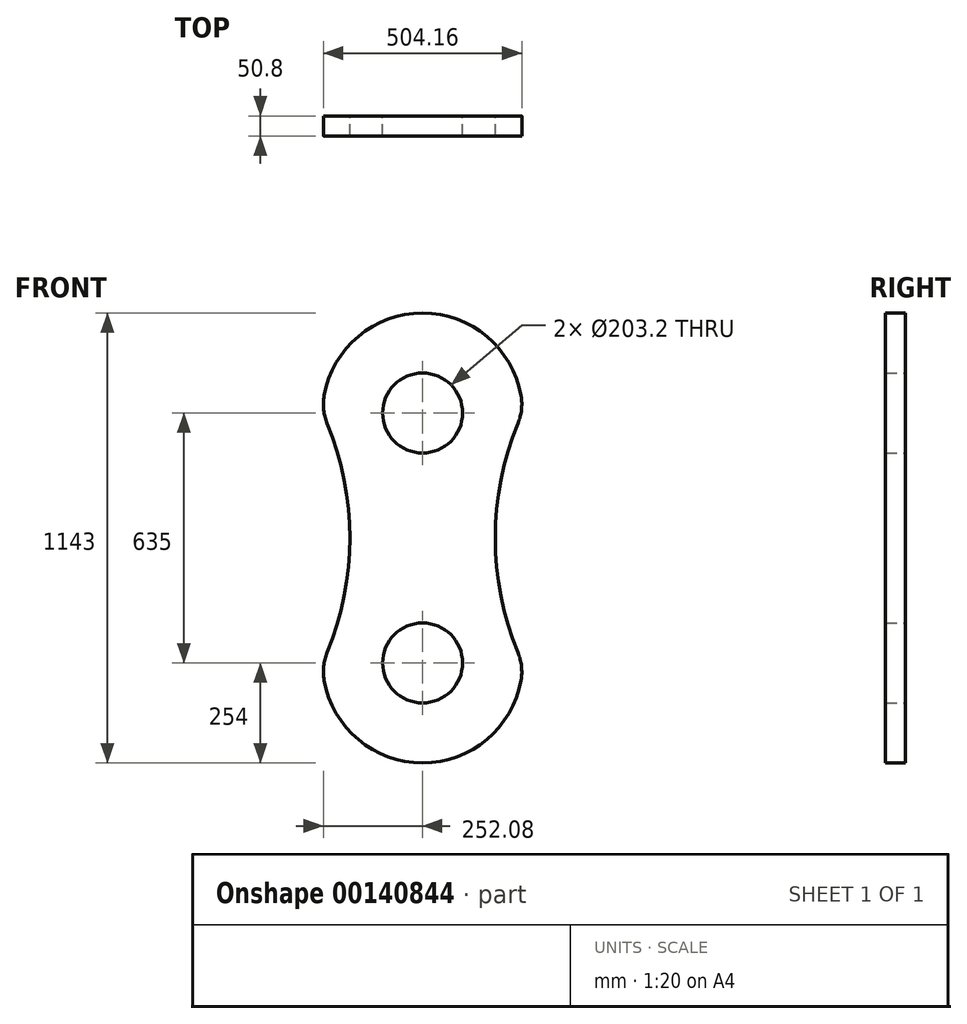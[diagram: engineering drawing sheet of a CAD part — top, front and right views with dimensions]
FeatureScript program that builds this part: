
annotation { "Feature Type Name" : "Feature", "Feature Type Description" : "" }
export const myFeature = defineFeature(function(context is Context, id is Id, definition is map)
    precondition{}
    {
        {
            var Q0;
            Q0=qCreatedBy(makeId("Front.planeOp"),FACE);
            var sketch = newSketch(context, id + "F0", { "sketchPlane" : qUnion([Q0])});
            skLineSegment(sketch, "E0.bottom", {"start": v(254, 317.5) * mm, "end": v(-254, 317.5) * mm});
            skLineSegment(sketch, "E0.top", {"start": v(254, -317.5) * mm, "end": v(-254, -317.5) * mm});
            skPoint(sketch, "E0.middle", {"position": v(0, 0) * mm});
            skArc(sketch, "E1", {"start": v(254, 317.5) * mm, "mid": v(0, 571.5) * mm, "end": v(-254, 317.5) * mm});
            skArc(sketch, "E2", {"start": v(-254, -317.5) * mm, "mid": v(0, -571.5) * mm, "end": v(254, -317.5) * mm});
            skArc(sketch, "E3", {"start": v(254, 317.5) * mm, "mid": v(184.7, 0) * mm, "end": v(254, -317.5) * mm});
            skArc(sketch, "E4", {"start": v(-254, -317.5) * mm, "mid": v(-184.7, 0) * mm, "end": v(-254, 317.5) * mm});
            skCircle(sketch, "E5", {"center": v(0, 317.5) * mm, "radius": 101.6 * mm});
            skCircle(sketch, "E6", {"center": v(0, -317.5) * mm, "radius": 101.6 * mm});
            skSolve(sketch);
        }
        {
            var Q0;
            Q0=makeQuery(id+"F0.imprint","IMPRINT",FACE,{"disambiguationData":[TD([[makeQuery(id+"F0.imprint","IMPRINT",EDGE,{"derivedFrom":sQuery(id+"F0.wireOp",EDGE,"E0.bottom")}),-1.0]])]});
            var Q1;
            Q1=makeQuery(id+"F0.imprint","IMPRINT",FACE,{"disambiguationData":[TD([[makeQuery(id+"F0.imprint","IMPRINT",EDGE,{"derivedFrom":sQuery(id+"F0.wireOp",EDGE,"E0.bottom")}),1.0]])]});
            var Q2;
            Q2=makeQuery(id+"F0.imprint","IMPRINT",FACE,{"disambiguationData":[TD([[makeQuery(id+"F0.imprint","IMPRINT",EDGE,{"derivedFrom":sQuery(id+"F0.wireOp",EDGE,"E0.top")}),1.0]])]});
            extrude(context, id + "F1", {"entities" : qUnion([Q0, Q1, Q2]), "depth" : 50.8 * mm});
        }
        {
            var Q0;
            Q0=makeQuery(id+"F1.opExtrude","SWEPT_EDGE",EDGE,{"disambiguationData":[OSD([sQuery(id+"F0.wireOp",EDGE,"E0.top"),sQuery(id+"F0.wireOp",EDGE,"E2"),sQuery(id+"F0.wireOp",EDGE,"E4")])]});
            fillet(context, id + "F2", {"entities" : qUnion([Q0]), "radius" : 127 * mm, "tangentPropagation" : true, "allowEdgeOverflow" : false});
        }
        {
            var Q0;
            Q0=makeQuery(id+"F1.opExtrude","SWEPT_EDGE",EDGE,{"disambiguationData":[OSD([sQuery(id+"F0.wireOp",EDGE,"E0.bottom"),sQuery(id+"F0.wireOp",EDGE,"E1"),sQuery(id+"F0.wireOp",EDGE,"E4")])]});
            fillet(context, id + "F3", {"entities" : qUnion([Q0]), "radius" : 127 * mm, "tangentPropagation" : true, "allowEdgeOverflow" : false});
        }
        {
            var Q0;
            Q0=makeQuery(id+"F1.opExtrude","SWEPT_EDGE",EDGE,{"disambiguationData":[OSD([sQuery(id+"F0.wireOp",EDGE,"E0.bottom"),sQuery(id+"F0.wireOp",EDGE,"E1"),sQuery(id+"F0.wireOp",EDGE,"E3")])]});
            fillet(context, id + "F4", {"entities" : qUnion([Q0]), "radius" : 127 * mm, "tangentPropagation" : true, "allowEdgeOverflow" : false});
        }
        {
            var Q0;
            Q0=makeQuery(id+"F1.opExtrude","SWEPT_EDGE",EDGE,{"disambiguationData":[OSD([sQuery(id+"F0.wireOp",EDGE,"E0.top"),sQuery(id+"F0.wireOp",EDGE,"E2"),sQuery(id+"F0.wireOp",EDGE,"E3")])]});
            fillet(context, id + "F5", {"entities" : qUnion([Q0]), "radius" : 127 * mm, "tangentPropagation" : true, "allowEdgeOverflow" : false});
        }
    });
